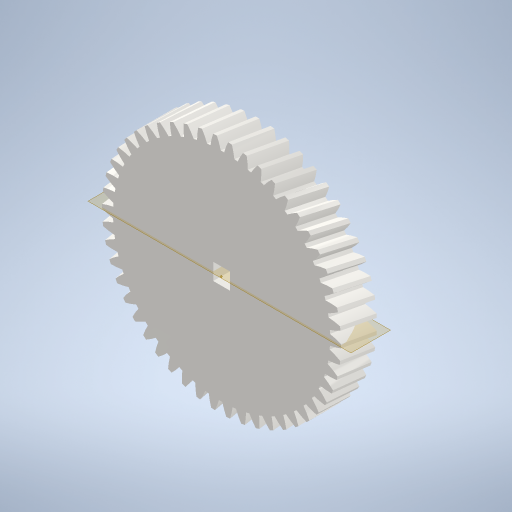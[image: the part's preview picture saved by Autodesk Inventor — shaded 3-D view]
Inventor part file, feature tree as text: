
AUTODESK INVENTOR PART (.ipt)
format: ipt  version: 2023.2 (Build 272271030, 271C)  size: 843,776 bytes
history: native  units: mm (DEFAULTED — no unit token found)
features: plane x5, other x4, sketch x4, extrude x3
ambient origin geometry x8: Origin, YZ Plane, XZ Plane, XY Plane, X Axis, Y Axis, Z Axis, Center Point
bodies: Solid1 (feature_tree)
feature tree (16):
  extrude  "Extrusion1"  Depth=10.0mm TaperAngle=0.0deg
  plane  "Work Plane1"
  plane  "Work Plane2"
  plane  "Work Plane3"
  other  "Spur Gear"
  extrude  "Extrusion2"  Depth=76.2mm TaperAngle=0.0deg
  other  "Work Point2"
  sketch  "Sketch4"  dims[d14=0.0mm d15=42.556529mm d16=0.0mm d17=0.0mm d18=0.0mm d19=42.556529mm d20=6.55mm d21=25.4mm d22=0.0mm d23=2.0mm d24=2.0mm d25=2.0mm d27=3.0mm d28=25.4mm d29=0.0mm d30=2.0mm]
  plane  "Work Plane7"
  extrude  "Extrusion3"  TaperAngle=0.0deg  [1 undecoded]
  sketch  "Sketch1"  dims[d0=66.51159mm d1=10.0mm d2=0.0mm]
  sketch  "Sketch2"  dims[d3=64.47959mm d4=76.2mm d5=0.0mm]
  other  "Srf1"
  sketch  "Sketch3"  dims[d6=0.0mm d7=0.628319mm d9=0.0mm]
  plane  "Work Plane4"
  other  "Pitch Diameter"
note: 1 required parameter value undecoded (feature->parameter linkage not recoverable at this tier; creation-order binding heuristic only, values carry confidence <= 0.55)
